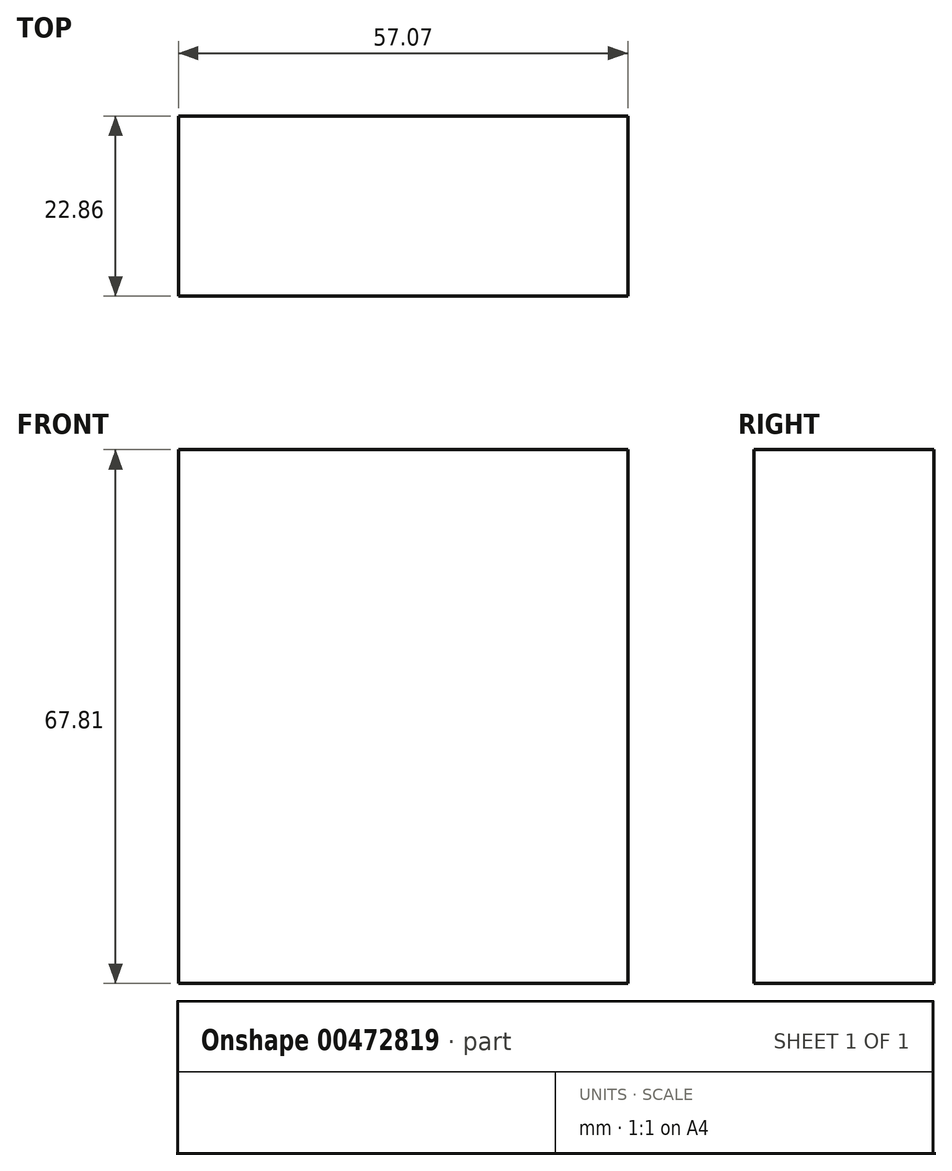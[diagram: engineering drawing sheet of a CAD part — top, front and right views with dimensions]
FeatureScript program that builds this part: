
annotation { "Feature Type Name" : "Feature", "Feature Type Description" : "" }
export const myFeature = defineFeature(function(context is Context, id is Id, definition is map)
    precondition{}
    {
        {
            var Q0;
            Q0=qCreatedBy(makeId("Front.planeOp"),FACE);
            var sketch = newSketch(context, id + "F0", { "sketchPlane" : qUnion([Q0])});
            skLineSegment(sketch, "E0.bottom", {"start": v(-27.66, 8.26) * mm, "end": v(-84.73, 8.26) * mm});
            skLineSegment(sketch, "E0.top", {"start": v(-27.66, 76.07) * mm, "end": v(-84.73, 76.07) * mm});
            skLineSegment(sketch, "E0.left", {"start": v(-27.66, 8.26) * mm, "end": v(-27.66, 76.07) * mm});
            skLineSegment(sketch, "E0.right", {"start": v(-84.73, 8.26) * mm, "end": v(-84.73, 76.07) * mm});
            skPoint(sketch, "E0.middle", {"position": v(-56.2, 42.17) * mm});
            skSolve(sketch);
        }
        {
            var Q0;
            Q0=makeQuery(id+"F0.imprint","IMPRINT",FACE,{"disambiguationData":[TD([[makeQuery(id+"F0.imprint","IMPRINT",EDGE,{"derivedFrom":sQuery(id+"F0.wireOp",EDGE,"E0.bottom")}),-1.0]])]});
            extrude(context, id + "F1", {"entities" : qUnion([Q0]), "depth" : 22.86 * mm});
        }
    });
